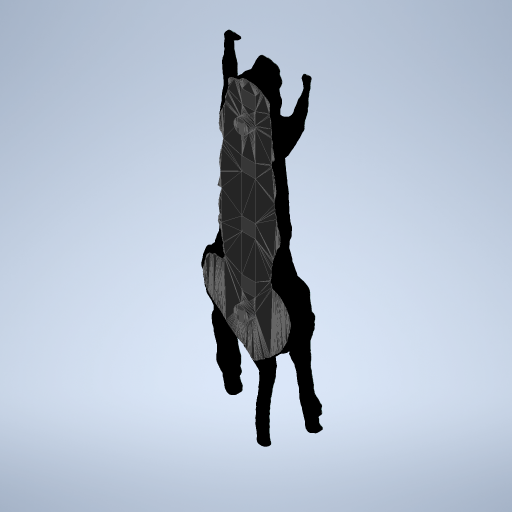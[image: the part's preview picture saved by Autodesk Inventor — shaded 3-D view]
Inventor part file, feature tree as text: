
AUTODESK INVENTOR PART (.ipt)
format: ipt  version: 2023 (Build 270158000, 158)  size: 2,342,912 bytes
history: native  units: in
note: dims shown in document units (in); Inventor stores cm internally (conversion verified against a paired STEP export)
features: other x2, extrude x1, sketch x1
ambient origin geometry x8: Origin, YZ Plane, XZ Plane, XY Plane, X Axis, Y Axis, Z Axis, Center Point
bodies: Solid1 (feature_tree)
feature tree (4):
  other  "prone_mouse_bottom_TLD"
  extrude  "Extrusion1"  Depth=0.0472in
  sketch  "Sketch1"  dims[d0=0.0472in d1=0.0in d2=0.0197in d3=0.0344in]
  other  "MeshFeature1"
